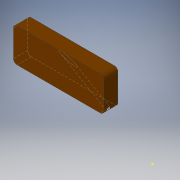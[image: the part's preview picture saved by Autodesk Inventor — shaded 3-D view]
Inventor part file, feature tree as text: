
AUTODESK INVENTOR PART (.ipt)
format: ipt  version: 2018 (Build 220112000, 112)  size: 379,392 bytes
history: native  units: in
note: dims shown in document units (in); Inventor stores cm internally (conversion verified against a paired STEP export)
features: other x4, extrude x1, boolean_combine x1, sketch x1, projected_geometry x1
ambient origin geometry x8: Origin, YZ Plane, XZ Plane, XY Plane, X Axis, Y Axis, Z Axis, Center Point
bodies: Solid1 (feature_tree), Solid2 (feature_tree)
feature tree (8):
  other  "drill back cavity to neck pickup cavity hole.iam"
  other  "Body.ipt:1"
  other  "Drill 12.ipt:1"
  extrude  "Extrusion1"  Depth=0.3937in TaperAngle=0.0deg
  boolean_combine  "Combine1"
  other  "Work Point1"
  sketch  "Sketch1"  dims[d0=0.3937in d1=1.0in d2=0.0in]
  projected_geometry  "Projected Loop1"
